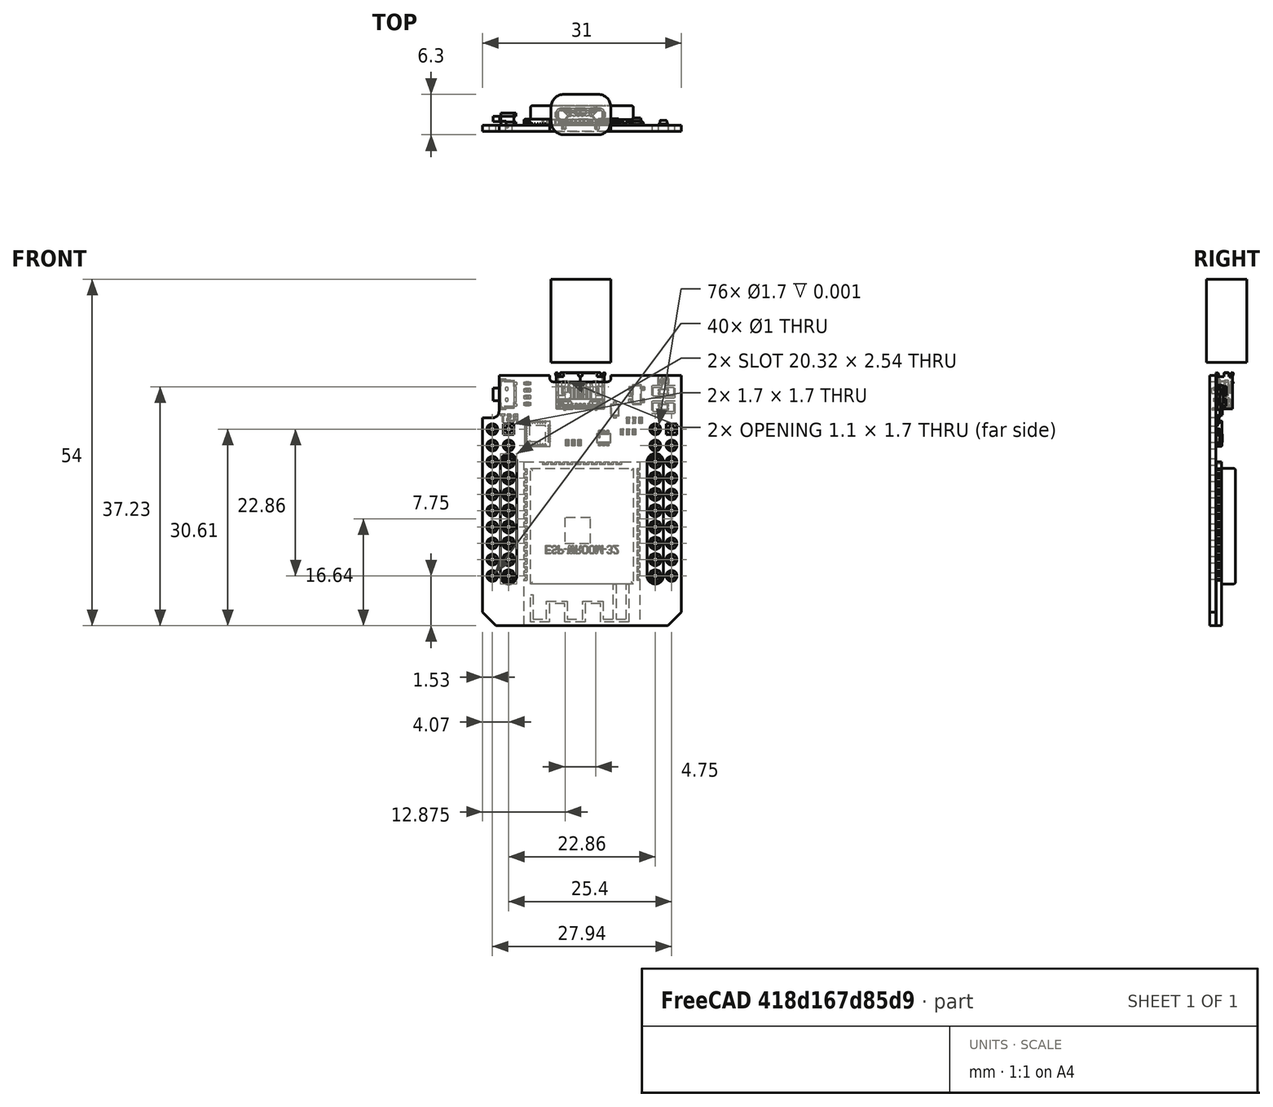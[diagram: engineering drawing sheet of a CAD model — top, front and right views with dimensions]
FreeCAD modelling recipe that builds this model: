
FCSTD DOCUMENT  (FreeCAD 0.18R16117 (Git))
Label: esp32-mh-et-live-minikit-d1
License: All rights reserved
LicenseURL: http://en.wikipedia.org/wiki/All_rights_reserved
objects: Part::Feature×1, Sketcher::SketchObject×1, PartDesign::Pad×1, PartDesign::Body×1
note: 5 computed .brp shape members not serialized (recipe doc carries the construction recipe); baked Part::Feature solids carry a one-line shape summary decoded from their .brp

FEATURE [Part::Feature] Part__Feature  label="MH-ET_LIVE_MiniKit"
  shape: bbox 31.02 x 99.68 x 39.44 mm, 5494 faces, 23 solids (baked)
FEATURE [Sketcher::SketchObject] Sketch
  AttachmentOffset = pos=(0,0,21.5) rot=(0,0,1;0rad)
  MapMode = 5
  Placement = pos=(0,0,21.5) rot=(0,0,1;0rad)
  Support = -> [XY_Plane]
  sketch-geometry (8):
    g0: LineSegment StartX=-2.8 StartY=5.8 StartZ=0 EndX=2.5 EndY=5.8 EndZ=0
    g1: LineSegment StartX=4.5 StartY=3.8 StartZ=0 EndX=4.5 EndY=1.5 EndZ=0
    g2: LineSegment StartX=2.5 StartY=-0.5 StartZ=0 EndX=-2.8 EndY=-0.5 EndZ=0
    g3: LineSegment StartX=-4.8 StartY=1.5 StartZ=0 EndX=-4.8 EndY=3.8 EndZ=0
    g4: ArcOfCircle CenterX=2.5 CenterY=1.5 CenterZ=0 NormalX=0 NormalY=0 NormalZ=1 AngleXU=0 Radius=2 StartAngle=4.71239 EndAngle=6.28319
    g5: ArcOfCircle CenterX=2.5 CenterY=3.8 CenterZ=0 NormalX=0 NormalY=0 NormalZ=1 AngleXU=0 Radius=2 StartAngle=0 EndAngle=1.5708
    g6: ArcOfCircle CenterX=-2.8 CenterY=3.8 CenterZ=0 NormalX=0 NormalY=0 NormalZ=1 AngleXU=0 Radius=2 StartAngle=1.5708 EndAngle=3.14159
    g7: ArcOfCircle CenterX=-2.8 CenterY=1.5 CenterZ=0 NormalX=0 NormalY=0 NormalZ=1 AngleXU=0 Radius=2 StartAngle=3.14159 EndAngle=4.71239
  constraints (20):
    c: Horizontal(g2)
    c: Vertical(g1)
    c: Vertical(g3)
    c: Tangent(g2,g4) = 1.5708
    c: Tangent(g1,g4) = 1.5708
    c: Tangent(g1,g5) = 1.5708
    c: Tangent(g0,g5) = 1.5708
    c: Tangent(g0,g6) = 1.5708
    c: Tangent(g3,g6) = 1.5708
    c: Tangent(g3,g7) = 1.5708
    c: Tangent(g2,g7) = 1.5708
    c: Equal(g7,g4)
    c: Equal(g4,g5)
    c: Equal(g5,g6)
    c: DistanceX(g3,g1) = 9.3
    c: DistanceY(g2,g0) = 6.3
    c: DistanceY(g-1,g2) = -0.5
    c: DistanceX(g1) = 4.5
    c: Radius(g5) = 2
    c: Horizontal(g0)
FEATURE [PartDesign::Pad] Pad
  Length = 13
  Length2 = 100
  Profile = -> Sketch
  Type = 0
FEATURE [PartDesign::Body] Body
  Group = -> [Sketch,Pad]
  Origin = -> Origin
  Tip = -> Pad
